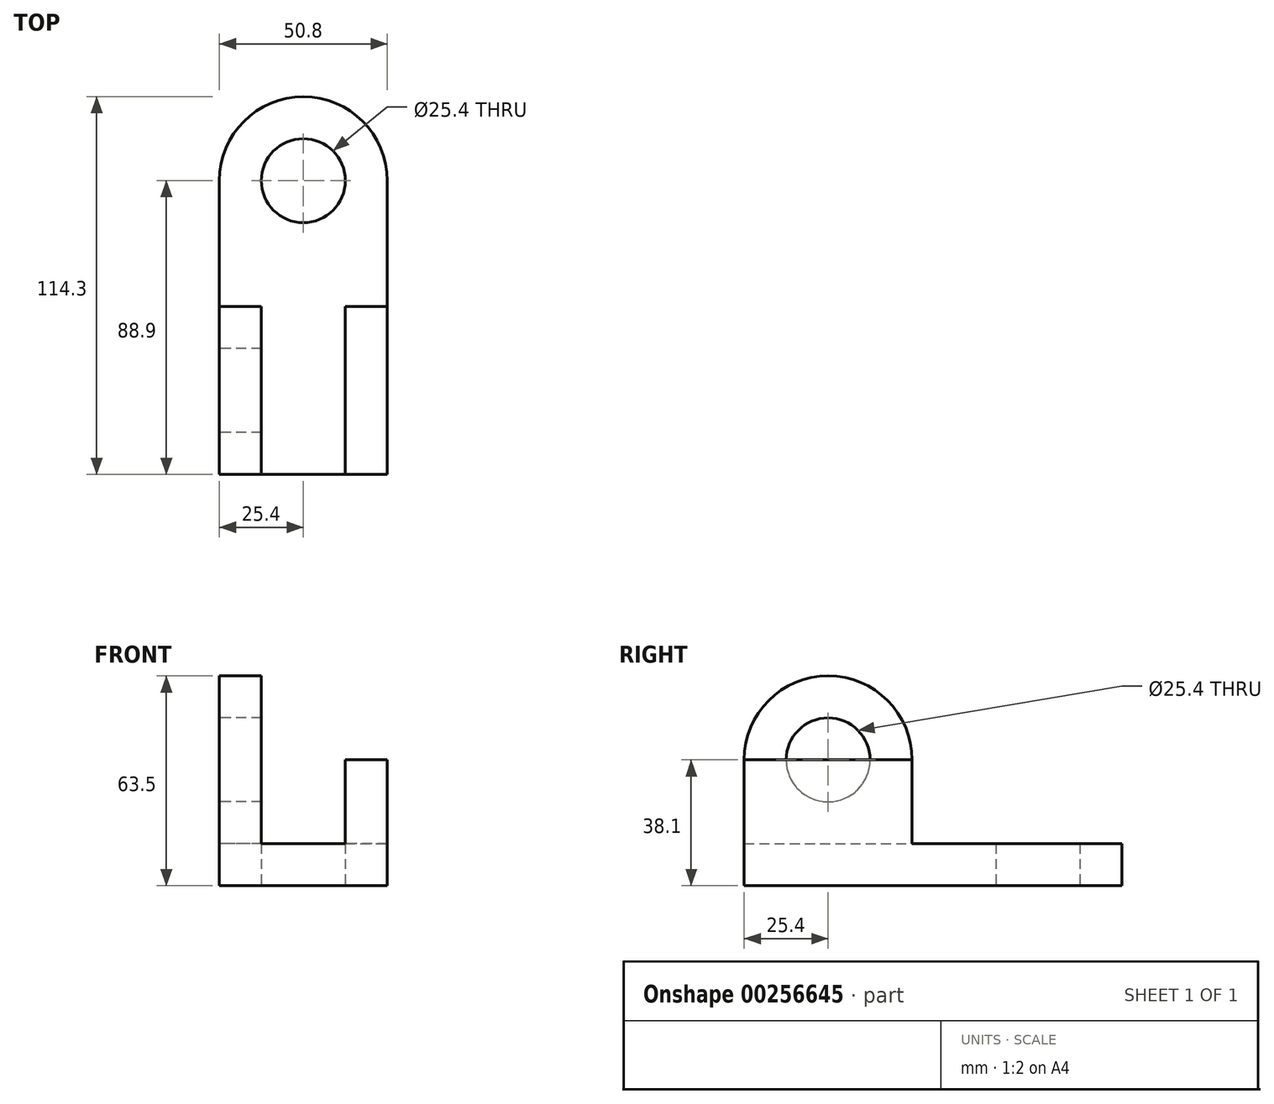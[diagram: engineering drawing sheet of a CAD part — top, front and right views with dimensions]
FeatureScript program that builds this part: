
annotation { "Feature Type Name" : "Feature", "Feature Type Description" : "" }
export const myFeature = defineFeature(function(context is Context, id is Id, definition is map)
    precondition{}
    {
        {
            var Q0;
            Q0=qCreatedBy(makeId("Top.planeOp"),FACE);
            var sketch = newSketch(context, id + "F0", { "sketchPlane" : qUnion([Q0])});
            skArc(sketch, "E0", {"start": v(25.4, 0) * mm, "mid": v(0, 25.4) * mm, "end": v(-25.4, 0) * mm});
            skCircle(sketch, "E1", {"center": v(0, 0) * mm, "radius": 12.7 * mm});
            skLineSegment(sketch, "E2", {"start": v(-25.4, 0) * mm, "end": v(-25.4, -88.9) * mm});
            skLineSegment(sketch, "E3", {"start": v(25.4, 0) * mm, "end": v(25.4, -88.9) * mm});
            skLineSegment(sketch, "E4", {"start": v(-25.4, -88.9) * mm, "end": v(25.4, -88.9) * mm});
            skLineSegment(sketch, "E5", {"start": v(0, 0) * mm, "end": v(0, -88.9) * mm, "construction": true});
            skLineSegment(sketch, "E6", {"start": v(-12.7, -88.9) * mm, "end": v(-12.7, -38.1) * mm});
            skLineSegment(sketch, "E7.MirrorCS", {"start": v(12.7, -88.9) * mm, "end": v(12.7, -38.1) * mm});
            skLineSegment(sketch, "E8", {"start": v(-12.7, -38.1) * mm, "end": v(-25.4, -38.1) * mm});
            skLineSegment(sketch, "E9", {"start": v(12.7, -38.1) * mm, "end": v(25.4, -38.1) * mm});
            skSolve(sketch);
        }
        {
            var Q0;
            {var subQ1=sQuery(id+"F0.wireOp",EDGE,"E0");Q0=makeQuery(id+"F0.imprint","IMPRINT",FACE,{"disambiguationData":[TD([[makeQuery(id+"F0.imprint","IMPRINT",EDGE,{"derivedFrom":subQ1}),1.0]])]});}
            extrude(context, id + "F1", {"entities" : qUnion([Q0]), "depth" : 12.7 * mm});
        }
        {
            var Q0;
            {var subQ4=sQuery(id+"F0.wireOp",EDGE,"E6");Q0=makeQuery(id+"F0.imprint","IMPRINT",FACE,{"disambiguationData":[TD([[makeQuery(id+"F0.imprint","IMPRINT",EDGE,{"derivedFrom":subQ4}),1.0]])]});}
            var Q1;
            {var subQ4=sQuery(id+"F0.wireOp",EDGE,"E7.MirrorCS");Q1=makeQuery(id+"F0.imprint","IMPRINT",FACE,{"disambiguationData":[TD([[makeQuery(id+"F0.imprint","IMPRINT",EDGE,{"derivedFrom":subQ4}),-1.0]])]});}
            extrude(context, id + "F2", {"entities" : qUnion([Q0, Q1]), "operationType" : NewBodyOperationType.ADD, "depth" : 38.1 * mm});
        }
        {
            var Q0;
            {var subQ0=sQuery(id+"F0.wireOp",EDGE,"E2");Q0=makeQuery(id+"F2.boolean.opBoolean","MERGE",FACE,{"derivedFrom":[makeQuery(id+"F1.opExtrude","SWEPT_FACE",FACE,{"disambiguationData":[OSD([subQ0])]}),makeQuery(id+"F2.opExtrude","SWEPT_FACE",FACE,{"disambiguationData":[OSD([subQ0])]})]});}
            var sketch = newSketch(context, id + "F3", { "sketchPlane" : qUnion([Q0])});
            skCircle(sketch, "E10", {"center": v(63.5, 38.1) * mm, "radius": 25.4 * mm});
            skCircle(sketch, "E11", {"center": v(63.5, 38.1) * mm, "radius": 12.7 * mm});
            skSolve(sketch);
        }
        {
            var Q0;
            {var subQ1=sQuery(id+"F0.wireOp",EDGE,"E2");var subQ2=makeQuery(id+"F2.opExtrude","CAP_EDGE",EDGE,{"disambiguationData":[OSD([subQ1])],"isStart":false});var subQ5=sQuery(id+"F3.wireOp",EDGE,"E11");var subQ6=makeQuery(id+"F3.imprint","INTERSECT",VERTEX,{"disambiguationData":[OD(0.0)],"derivedFrom":[subQ2,subQ5]});Q0=makeQuery(id+"F3.imprint","IMPRINT",FACE,{"disambiguationData":[TD([[makeQuery(id+"F3.imprint","IMPRINT",EDGE,{"disambiguationData":[TD([[subQ6,-1.0]])],"derivedFrom":subQ5}),-1.0]])]});}
            extrude(context, id + "F4", {"entities" : qUnion([Q0]), "operationType" : NewBodyOperationType.ADD, "oppositeDirection" : true, "depth" : 12.7 * mm});
        }
        {
            var Q0;
            {var subQ0=sQuery(id+"F3.wireOp",EDGE,"E11");var subQ1=makeQuery(id+"F2.opExtrude","CAP_EDGE",EDGE,{"disambiguationData":[OSD([sQuery(id+"F0.wireOp",EDGE,"E2")])],"isStart":false});var subQ2=makeQuery(id+"F3.imprint","INTERSECT",VERTEX,{"disambiguationData":[OD(0.0)],"derivedFrom":[subQ1,subQ0]});Q0=makeQuery(id+"F3.imprint","IMPRINT",FACE,{"disambiguationData":[TD([[makeQuery(id+"F3.imprint","IMPRINT",EDGE,{"disambiguationData":[TD([[subQ2,1.0]])],"derivedFrom":subQ0}),1.0]])]});}
            extrude(context, id + "F5", {"entities" : qUnion([Q0]), "operationType" : NewBodyOperationType.REMOVE, "oppositeDirection" : true, "depth" : 12.7 * mm});
        }
        {
            var Q0;
            {var subQ0=sQuery(id+"F0.wireOp",EDGE,"E3");Q0=makeQuery(id+"F2.boolean.opBoolean","MERGE",FACE,{"derivedFrom":[makeQuery(id+"F1.opExtrude","SWEPT_FACE",FACE,{"disambiguationData":[OSD([subQ0])]}),makeQuery(id+"F2.opExtrude","SWEPT_FACE",FACE,{"disambiguationData":[OSD([subQ0])]})]});}
            var sketch = newSketch(context, id + "F6", { "sketchPlane" : qUnion([Q0])});
            skCircle(sketch, "E12", {"center": v(-63.5, 38.1) * mm, "radius": 25.4 * mm});
            skCircle(sketch, "E13", {"center": v(-63.5, 38.1) * mm, "radius": 12.7 * mm});
            skSolve(sketch);
        }
        {
            var Q0;
            {var subQ1=sQuery(id+"F0.wireOp",EDGE,"E3");var subQ2=makeQuery(id+"F2.opExtrude","CAP_EDGE",EDGE,{"disambiguationData":[OSD([subQ1])],"isStart":false});var subQ5=sQuery(id+"F6.wireOp",EDGE,"E13");var subQ7=makeQuery(id+"F6.imprint","INTERSECT",VERTEX,{"disambiguationData":[OD(0.0)],"derivedFrom":[subQ2,subQ5]});Q0=makeQuery(id+"F6.imprint","IMPRINT",FACE,{"disambiguationData":[TD([[makeQuery(id+"F6.imprint","IMPRINT",EDGE,{"disambiguationData":[TD([[subQ7,1.0]])],"derivedFrom":subQ5}),-1.0]])]});}
            extrude(context, id + "F7", {"entities" : qUnion([Q0]), "operationType" : NewBodyOperationType.ADD, "oppositeDirection" : true, "depth" : 12.7 * mm});
        }
        {
            var Q0;
            {var subQ0=sQuery(id+"F6.wireOp",EDGE,"E13");var subQ1=makeQuery(id+"F2.opExtrude","CAP_EDGE",EDGE,{"disambiguationData":[OSD([sQuery(id+"F0.wireOp",EDGE,"E3")])],"isStart":false});var subQ2=makeQuery(id+"F6.imprint","INTERSECT",VERTEX,{"disambiguationData":[OD(0.0)],"derivedFrom":[subQ1,subQ0]});Q0=makeQuery(id+"F6.imprint","IMPRINT",FACE,{"disambiguationData":[TD([[makeQuery(id+"F6.imprint","IMPRINT",EDGE,{"disambiguationData":[TD([[subQ2,-1.0]])],"derivedFrom":subQ0}),1.0]])]});}
            extrude(context, id + "F8", {"entities" : qUnion([Q0]), "operationType" : NewBodyOperationType.REMOVE, "oppositeDirection" : true, "depth" : 12.7 * mm});
        }
    });
